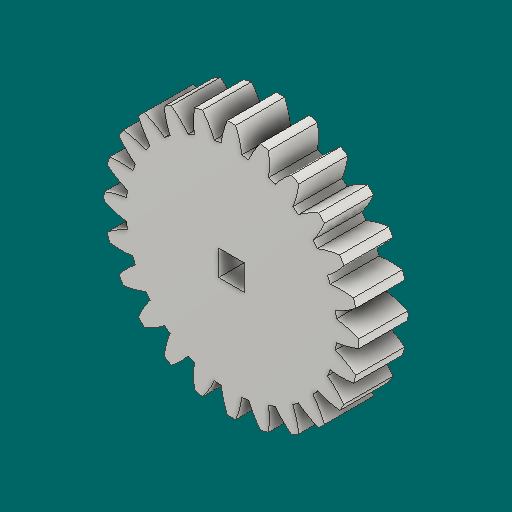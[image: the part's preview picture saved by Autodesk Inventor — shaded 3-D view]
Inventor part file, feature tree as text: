
AUTODESK INVENTOR PART (.ipt)
format: ipt  version: 2023.1 (Build 271208000, 208)  size: 261,632 bytes
history: native  units: mm (DEFAULTED — no unit token found)
features: plane x3, other x3, sketch x3, extrude x2
ambient origin geometry x8: Origin, YZ Plane, XZ Plane, XY Plane, X Axis, Y Axis, Z Axis, Center Point
bodies: Solid1 (feature_tree)
feature tree (11):
  extrude  "Extrusion1"  Depth=6.35mm TaperAngle=0.0deg
  plane  "Work Plane1"
  plane  "Work Plane2"
  plane  "Work Plane3"
  other  "Spur Gear"
  extrude  "Extrusion2"  Depth=76.2mm TaperAngle=0.0deg
  sketch  "Sketch1"  dims[d0=33.02mm d1=6.35mm d2=0.0mm]
  sketch  "Sketch2"  dims[d3=30.48mm d4=76.2mm d5=0.0mm]
  other  "Srf1"
  sketch  "Sketch3"  dims[d6=0.0mm d7=1.308997mm d9=0.0mm d14=0.0mm d15=30.48mm d16=0.0mm d17=0.0mm d18=0.0mm d19=30.48mm d20=3.302mm d21=3.302mm d22=25.4mm d23=0.0mm]
  other  "Pitch Diameter"
